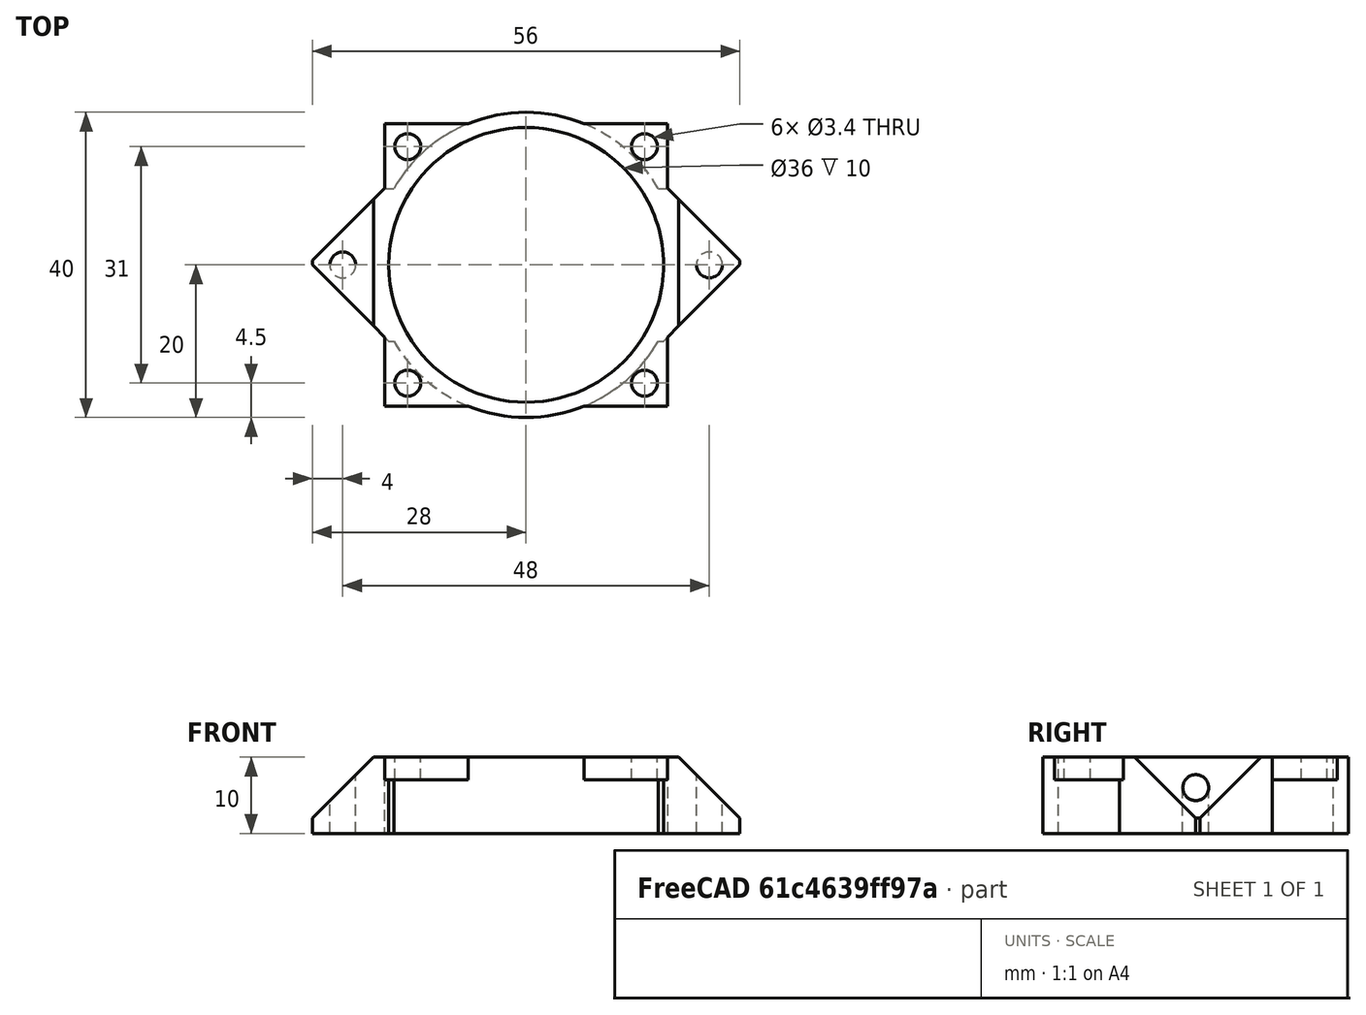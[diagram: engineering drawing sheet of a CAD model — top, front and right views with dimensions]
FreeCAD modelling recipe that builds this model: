
FCSTD DOCUMENT
Label: Lüfterhalter
objects: Part::Cylinder×8, Part::Box×5, Part::MultiFuse×4, Part::Cut×4, Part::MultiCommon×1
note: 22 computed .brp shape members not serialized (recipe doc carries the construction recipe); baked Part::Feature solids carry a one-line shape summary decoded from their .brp

FEATURE [Part::Cylinder] Cylinder  label="Bohrung 001"
  Angle = 360
  Height = 10
  Radius = 1.7
FEATURE [Part::Cylinder] Cylinder001  label="Bohrung 002"
  Angle = 360
  Height = 10
  Placement = pos=(31,0,0) rot=(0,0,1;0rad)
  Radius = 1.7
FEATURE [Part::Cylinder] Cylinder002  label="Bohrung 003"
  Angle = 360
  Height = 10
  Placement = pos=(31,31,0) rot=(0,0,1;0rad)
  Radius = 1.7
FEATURE [Part::Cylinder] Cylinder003  label="Bohrung 004"
  Angle = 360
  Height = 10
  Placement = pos=(0,31,0) rot=(0,0,1;0rad)
  Radius = 1.7
FEATURE [Part::MultiFuse] Fusion  label="Bohrungen für Lüfter oben"
  Placement = pos=(-15.5,-15.5,0) rot=(0,0,1;0rad)
  Shapes = -> [Cylinder,Cylinder002,Cylinder001,Cylinder003]
FEATURE [Part::Cylinder] Cylinder004  label="Kanal"
  Angle = 360
  Height = 10
  Radius = 18
FEATURE [Part::Cylinder] Cylinder005  label="Basis"
  Angle = 360
  Height = 10
  Radius = 20
FEATURE [Part::Box] Box  label="Halter oben"
  Height = 3
  Length = 37
  Placement = pos=(-18.5,-18.5,7) rot=(0,0,1;0rad)
  Width = 37
FEATURE [Part::Box] Box001  label="Halter unten Basis"
  Height = 10
  Length = 40
  Placement = pos=(0,-28,0) rot=(0,0,1;0.785397rad)
  Width = 40
FEATURE [Part::Cylinder] Cylinder006  label="Bohrung 005"
  Angle = 360
  Height = 10
  Placement = pos=(-24,0,0) rot=(0,0,1;0rad)
  Radius = 1.7
FEATURE [Part::Cylinder] Cylinder007  label="Bohrung 006"
  Angle = 360
  Height = 10
  Placement = pos=(24,0,0) rot=(0,0,1;0rad)
  Radius = 1.7
FEATURE [Part::Box] Box002  label="Halter unten Zuschnitt"
  Height = 10
  Length = 56
  Placement = pos=(-28,-10,0) rot=(0,0,1;0rad)
  Width = 20
FEATURE [Part::MultiFuse] Fusion001  label="Buhrungen unten"
  Shapes = -> [Cylinder007,Cylinder006]
FEATURE [Part::Cut] Cut001  label="Halter oben mit Bohrungen"
  Base = -> Box
  Tool = -> Fusion
FEATURE [Part::Box] Box003  label="Abschnitt 1"
  Height = 10
  Length = 20
  Placement = pos=(15,-10,15) rot=(0,1,0;0.785397rad)
  Width = 20
FEATURE [Part::Box] Box004  label="Abschnitt 002"
  Height = 10
  Length = 20
  Placement = pos=(-30,-10,0) rot=(0,-1,0;0.785397rad)
  Width = 20
FEATURE [Part::MultiFuse] Fusion002  label="Abschnitt"
  Shapes = -> [Box003,Box004]
FEATURE [Part::Cut] Cut  label="Halter unten Zuschnitt001"
  Base = -> Box002
  Tool = -> Fusion002
FEATURE [Part::MultiCommon] Common  label="Halter unten"
  Shapes = -> [Box001,Cut]
FEATURE [Part::Cut] Cut002  label="Halter unten mit Bohrungen"
  Base = -> Common
  Tool = -> Fusion001
FEATURE [Part::MultiFuse] Fusion003  label="Basis mit Haltern"
  Shapes = -> [Cut002,Cut001,Cylinder005]
FEATURE [Part::Cut] Cut003  label="Lüfterhalter"
  Base = -> Fusion003
  Tool = -> Cylinder004
